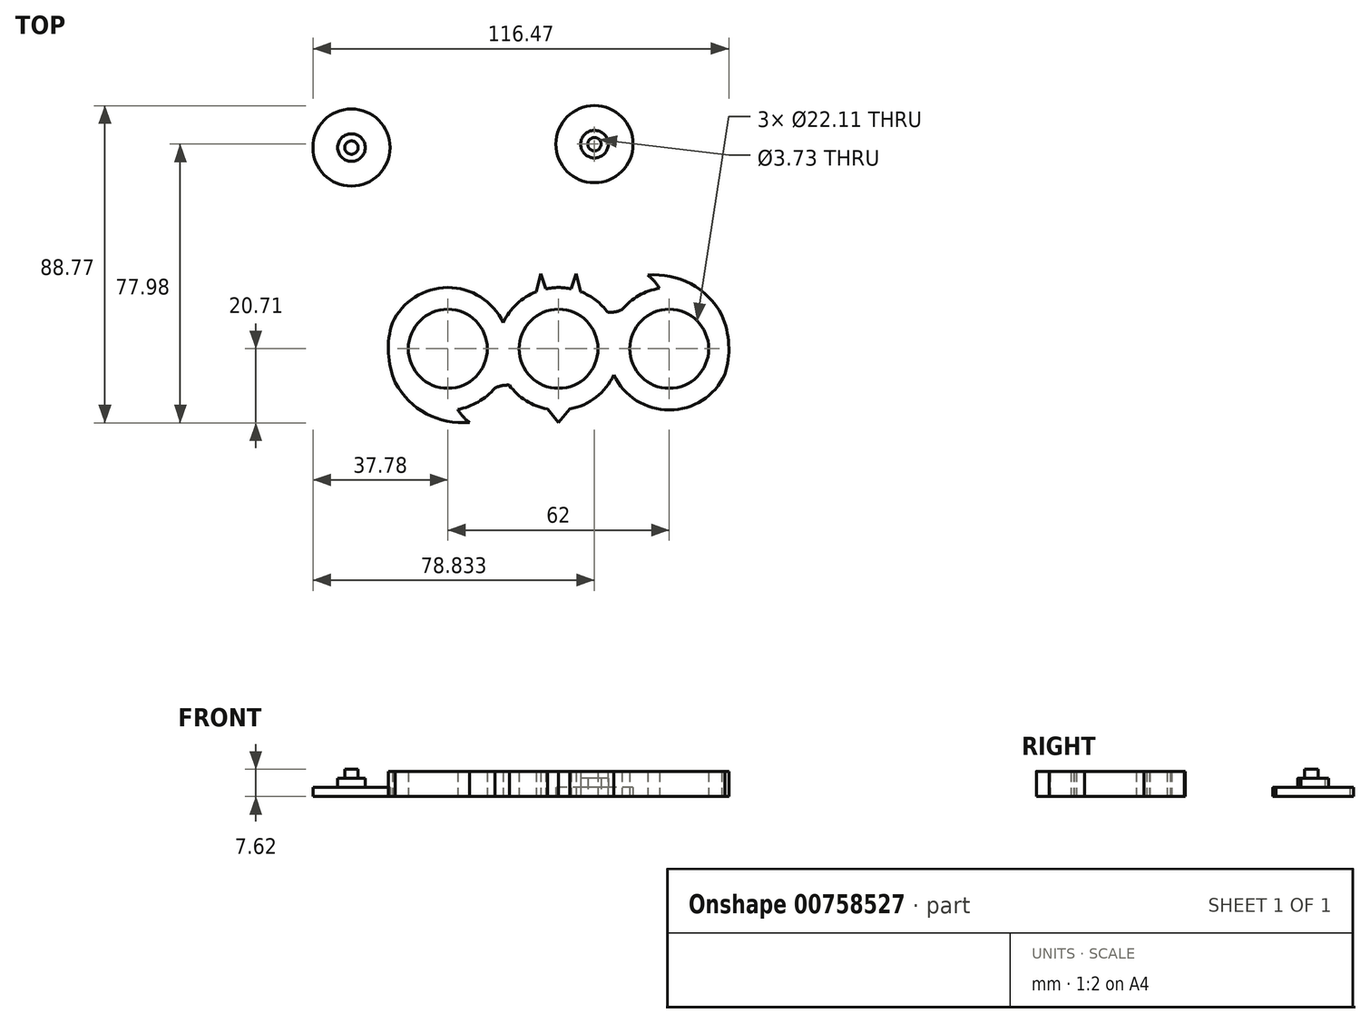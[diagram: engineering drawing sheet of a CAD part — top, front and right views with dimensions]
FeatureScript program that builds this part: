
annotation { "Feature Type Name" : "Feature", "Feature Type Description" : "" }
export const myFeature = defineFeature(function(context is Context, id is Id, definition is map)
    precondition{}
    {
        {
            var Q0;
            Q0=qCreatedBy(makeId("Top.planeOp"),FACE);
            var sketch = newSketch(context, id + "F0", { "sketchPlane" : qUnion([Q0])});
            skCircle(sketch, "E0", {"center": v(31, 0) * mm, "radius": 11.05 * mm});
            skCircle(sketch, "E1", {"center": v(-31, 0) * mm, "radius": 11.05 * mm});
            skCircle(sketch, "E2", {"center": v(0, 0) * mm, "radius": 11.05 * mm});
            skCircle(sketch, "E3", {"center": v(-31, 0) * mm, "radius": 17.15 * mm});
            skCircle(sketch, "E4", {"center": v(31, 0) * mm, "radius": 17.15 * mm});
            skCircle(sketch, "E5", {"center": v(0, 0) * mm, "radius": 17.15 * mm});
            skArc(sketch, "E6", {"start": v(-28.25, 16.92) * mm, "mid": v(-26.8, 18.94) * mm, "end": v(-24.96, 20.62) * mm});
            skArc(sketch, "E7", {"start": v(-24.96, 20.62) * mm, "mid": v(-37.01, 18.18) * mm, "end": v(-45.7, 9.47) * mm});
            skArc(sketch, "E8.MirrorCS", {"start": v(-24.96, -20.62) * mm, "mid": v(-37.01, -18.18) * mm, "end": v(-45.7, -9.47) * mm});
            skArc(sketch, "E9.MirrorCS", {"start": v(-28.25, -16.92) * mm, "mid": v(-26.8, -18.94) * mm, "end": v(-24.96, -20.62) * mm});
            skArc(sketch, "E10.MirrorCS", {"start": v(28.25, 16.92) * mm, "mid": v(26.8, 18.94) * mm, "end": v(24.96, 20.62) * mm});
            skArc(sketch, "E11.MirrorCS", {"start": v(24.96, 20.62) * mm, "mid": v(37.01, 18.18) * mm, "end": v(45.7, 9.47) * mm});
            skArc(sketch, "E12.MirrorCS", {"start": v(24.96, -20.62) * mm, "mid": v(37.01, -18.18) * mm, "end": v(45.7, -9.47) * mm});
            skArc(sketch, "E13.MirrorCS", {"start": v(28.25, -16.92) * mm, "mid": v(26.8, -18.94) * mm, "end": v(24.96, -20.62) * mm});
            skLineSegment(sketch, "E14", {"start": v(-3.1, -16.86) * mm, "end": v(0, -20.62) * mm});
            skLineSegment(sketch, "E15", {"start": v(0, -20.62) * mm, "end": v(3.15, -16.85) * mm});
            skLineSegment(sketch, "E16", {"start": v(-6.23, 15.97) * mm, "end": v(-4.98, 20.95) * mm});
            skLineSegment(sketch, "E17", {"start": v(-4.98, 20.95) * mm, "end": v(-3.55, 16.77) * mm});
            skLineSegment(sketch, "E18.MirrorCS", {"start": v(4.98, 20.95) * mm, "end": v(3.55, 16.77) * mm});
            skLineSegment(sketch, "E19.MirrorCS", {"start": v(6.23, 15.97) * mm, "end": v(4.98, 20.95) * mm});
            skArc(sketch, "E20", {"start": v(-13.8, -10.17) * mm, "mid": v(-15.85, -10.33) * mm, "end": v(-17.8, -10.94) * mm});
            skArc(sketch, "E21.MirrorCS", {"start": v(13.8, -10.17) * mm, "mid": v(15.85, -10.33) * mm, "end": v(17.8, -10.94) * mm});
            skArc(sketch, "E22.MirrorCS", {"start": v(-13.8, 10.17) * mm, "mid": v(-15.85, 10.33) * mm, "end": v(-17.8, 10.94) * mm});
            skArc(sketch, "E23.MirrorCS", {"start": v(13.8, 10.17) * mm, "mid": v(15.85, 10.33) * mm, "end": v(17.8, 10.94) * mm});
            skArc(sketch, "E24", {"start": v(-45.7, 9.47) * mm, "mid": v(-47.69, 0) * mm, "end": v(-45.7, -9.47) * mm});
            skArc(sketch, "E25.MirrorCS", {"start": v(45.7, 9.47) * mm, "mid": v(47.69, 0) * mm, "end": v(45.7, -9.47) * mm});
            skSolve(sketch);
        }
        {
            var Q0;
            {var subQ0=sQuery(id+"F0.wireOp",EDGE,"E6");Q0=makeQuery(id+"F0.imprint","IMPRINT",FACE,{"disambiguationData":[TD([[makeQuery(id+"F0.imprint","IMPRINT",EDGE,{"derivedFrom":subQ0}),1.0]])]});}
            var Q1;
            {var subQ0=sQuery(id+"F0.wireOp",EDGE,"E9.MirrorCS");Q1=makeQuery(id+"F0.imprint","IMPRINT",FACE,{"disambiguationData":[TD([[makeQuery(id+"F0.imprint","IMPRINT",EDGE,{"derivedFrom":subQ0}),-1.0]])]});}
            var Q2;
            {var subQ0=sQuery(id+"F0.wireOp",EDGE,"E22.MirrorCS");Q2=makeQuery(id+"F0.imprint","IMPRINT",FACE,{"disambiguationData":[TD([[makeQuery(id+"F0.imprint","IMPRINT",EDGE,{"derivedFrom":subQ0}),1.0]])]});}
            var Q3;
            {var subQ0=sQuery(id+"F0.wireOp",EDGE,"E5");var subQ1=sQuery(id+"F0.wireOp",EDGE,"E3");var subQ2=makeQuery(id+"F0.imprint","INTERSECT",VERTEX,{"disambiguationData":[OD(0.0)],"derivedFrom":[subQ1,subQ0]});Q3=makeQuery(id+"F0.imprint","IMPRINT",FACE,{"disambiguationData":[TD([[makeQuery(id+"F0.imprint","IMPRINT",EDGE,{"disambiguationData":[TD([[subQ2,1.0]])],"derivedFrom":subQ1}),1.0]])]});}
            var Q4;
            {var subQ0=sQuery(id+"F0.wireOp",EDGE,"E20");Q4=makeQuery(id+"F0.imprint","IMPRINT",FACE,{"disambiguationData":[TD([[makeQuery(id+"F0.imprint","IMPRINT",EDGE,{"derivedFrom":subQ0}),-1.0]])]});}
            var Q5;
            Q5=makeQuery(id+"F0.imprint","IMPRINT",FACE,{"disambiguationData":[TD([[makeQuery(id+"F0.imprint","IMPRINT",EDGE,{"derivedFrom":sQuery(id+"F0.wireOp",EDGE,"E2")}),-1.0]])]});
            var Q6;
            {var subQ0=sQuery(id+"F0.wireOp",EDGE,"E16");Q6=makeQuery(id+"F0.imprint","IMPRINT",FACE,{"disambiguationData":[TD([[makeQuery(id+"F0.imprint","IMPRINT",EDGE,{"derivedFrom":subQ0}),-1.0]])]});}
            var Q7;
            {var subQ0=sQuery(id+"F0.wireOp",EDGE,"E18.MirrorCS");Q7=makeQuery(id+"F0.imprint","IMPRINT",FACE,{"disambiguationData":[TD([[makeQuery(id+"F0.imprint","IMPRINT",EDGE,{"derivedFrom":subQ0}),1.0]])]});}
            var Q8;
            {var subQ0=sQuery(id+"F0.wireOp",EDGE,"E14");Q8=makeQuery(id+"F0.imprint","IMPRINT",FACE,{"disambiguationData":[TD([[makeQuery(id+"F0.imprint","IMPRINT",EDGE,{"derivedFrom":subQ0}),1.0]])]});}
            var Q9;
            {var subQ0=sQuery(id+"F0.wireOp",EDGE,"E5");var subQ1=sQuery(id+"F0.wireOp",EDGE,"E4");var subQ2=makeQuery(id+"F0.imprint","INTERSECT",VERTEX,{"disambiguationData":[OD(0.0)],"derivedFrom":[subQ1,subQ0]});Q9=makeQuery(id+"F0.imprint","IMPRINT",FACE,{"disambiguationData":[TD([[makeQuery(id+"F0.imprint","IMPRINT",EDGE,{"disambiguationData":[TD([[subQ2,-1.0]])],"derivedFrom":subQ1}),1.0]])]});}
            var Q10;
            {var subQ0=sQuery(id+"F0.wireOp",EDGE,"E23.MirrorCS");Q10=makeQuery(id+"F0.imprint","IMPRINT",FACE,{"disambiguationData":[TD([[makeQuery(id+"F0.imprint","IMPRINT",EDGE,{"derivedFrom":subQ0}),-1.0]])]});}
            var Q11;
            {var subQ0=sQuery(id+"F0.wireOp",EDGE,"E21.MirrorCS");Q11=makeQuery(id+"F0.imprint","IMPRINT",FACE,{"disambiguationData":[TD([[makeQuery(id+"F0.imprint","IMPRINT",EDGE,{"derivedFrom":subQ0}),1.0]])]});}
            var Q12;
            Q12=makeQuery(id+"F0.imprint","IMPRINT",FACE,{"disambiguationData":[TD([[makeQuery(id+"F0.imprint","IMPRINT",EDGE,{"derivedFrom":sQuery(id+"F0.wireOp",EDGE,"E0")}),-1.0]])]});
            var Q13;
            {var subQ0=sQuery(id+"F0.wireOp",EDGE,"E10.MirrorCS");Q13=makeQuery(id+"F0.imprint","IMPRINT",FACE,{"disambiguationData":[TD([[makeQuery(id+"F0.imprint","IMPRINT",EDGE,{"derivedFrom":subQ0}),-1.0]])]});}
            var Q14;
            {var subQ0=sQuery(id+"F0.wireOp",EDGE,"E13.MirrorCS");Q14=makeQuery(id+"F0.imprint","IMPRINT",FACE,{"disambiguationData":[TD([[makeQuery(id+"F0.imprint","IMPRINT",EDGE,{"derivedFrom":subQ0}),1.0]])]});}
            var Q15;
            Q15=makeQuery(id+"F0.imprint","IMPRINT",FACE,{"disambiguationData":[TD([[makeQuery(id+"F0.imprint","IMPRINT",EDGE,{"derivedFrom":sQuery(id+"F0.wireOp",EDGE,"E1")}),-1.0]])]});
            extrude(context, id + "F1", {"entities" : qUnion([Q0, Q1, Q2, Q3, Q4, Q5, Q6, Q7, Q8, Q9, Q10, Q11, Q12, Q13, Q14, Q15]), "depth" : 7.04 * mm, "offsetDistance" : 25.4 * mm});
        }
        {
            var Q0;
            Q0=qCreatedBy(makeId("Top.planeOp"),FACE);
            var sketch = newSketch(context, id + "F2", { "sketchPlane" : qUnion([Q0])});
            skCircle(sketch, "E26", {"center": v(-57.99, 56.32) * mm, "radius": 10.8 * mm});
            skCircle(sketch, "E27", {"center": v(-57.99, 56.32) * mm, "radius": 3.86 * mm});
            skCircle(sketch, "E28", {"center": v(-57.99, 56.32) * mm, "radius": 1.87 * mm});
            skCircle(sketch, "E29", {"center": v(10.05, 57.27) * mm, "radius": 10.8 * mm});
            skCircle(sketch, "E30", {"center": v(10.05, 57.27) * mm, "radius": 3.86 * mm});
            skCircle(sketch, "E31", {"center": v(10.05, 57.27) * mm, "radius": 1.87 * mm});
            skSolve(sketch);
        }
        {
            var Q0;
            Q0=makeQuery(id+"F2.imprint","IMPRINT",FACE,{"disambiguationData":[TD([[makeQuery(id+"F2.imprint","IMPRINT",EDGE,{"derivedFrom":sQuery(id+"F2.wireOp",EDGE,"E27")}),1.0]])]});
            var Q1;
            Q1=makeQuery(id+"F2.imprint","IMPRINT",FACE,{"disambiguationData":[TD([[makeQuery(id+"F2.imprint","IMPRINT",EDGE,{"derivedFrom":sQuery(id+"F2.wireOp",EDGE,"E30")}),1.0]])]});
            extrude(context, id + "F3", {"entities" : qUnion([Q0, Q1]), "depth" : 5.08 * mm, "offsetDistance" : 25.4 * mm});
        }
        {
            var Q0;
            Q0 = qSketchRegion(id + "F2", true);
            extrude(context, id + "F4", {"entities" : qUnion([Q0]), "operationType" : NewBodyOperationType.ADD, "depth" : 2.54 * mm, "offsetDistance" : 25.4 * mm});
        }
        {
            var Q0;
            Q0=makeQuery(id+"F2.imprint","IMPRINT",FACE,{"disambiguationData":[TD([[makeQuery(id+"F2.imprint","IMPRINT",EDGE,{"derivedFrom":sQuery(id+"F2.wireOp",EDGE,"E28")}),1.0]])]});
            extrude(context, id + "F5", {"entities" : qUnion([Q0]), "operationType" : NewBodyOperationType.ADD, "depth" : 7.62 * mm, "offsetDistance" : 25.4 * mm});
        }
    });
